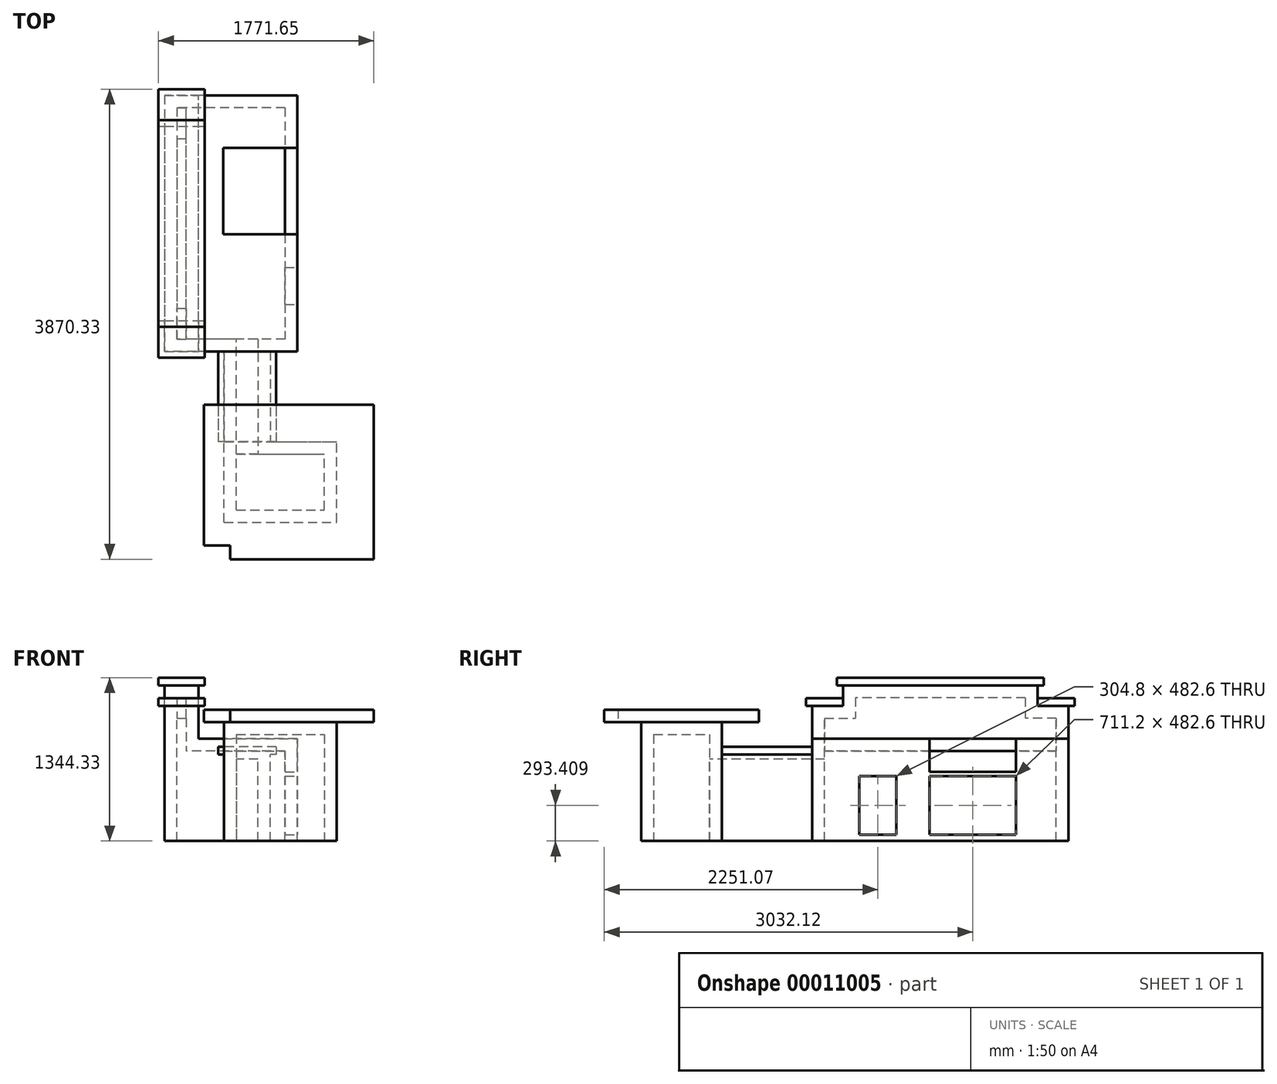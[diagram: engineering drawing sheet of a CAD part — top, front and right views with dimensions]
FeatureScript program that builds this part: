
annotation { "Feature Type Name" : "Feature", "Feature Type Description" : "" }
export const myFeature = defineFeature(function(context is Context, id is Id, definition is map)
    precondition{}
    {
        {
            var Q0;
            Q0=qCreatedBy(makeId("Top.planeOp"),FACE);
            var sketch = newSketch(context, id + "F0", { "sketchPlane" : qUnion([Q0])});
            skLineSegment(sketch, "E0.bottom", {"start": v(0, 0) * mm, "end": v(927.1, 0) * mm});
            skLineSegment(sketch, "E0.top", {"start": v(0, 663.58) * mm, "end": v(927.1, 663.58) * mm});
            skLineSegment(sketch, "E0.left", {"start": v(0, 0) * mm, "end": v(0, 663.57) * mm});
            skLineSegment(sketch, "E0.right", {"start": v(927.1, 0) * mm, "end": v(927.1, 663.57) * mm});
            skLineSegment(sketch, "E1", {"start": v(-165.1, 968.38) * mm, "end": v(1231.9, 968.38) * mm, "construction": true});
            skLineSegment(sketch, "E2", {"start": v(-165.1, 968.38) * mm, "end": v(-165.1, -536.51) * mm, "construction": true});
            skLineSegment(sketch, "E3", {"start": v(1231.9, 968.38) * mm, "end": v(1231.9, -304.8) * mm, "construction": true});
            skLineSegment(sketch, "E4", {"start": v(-360.43, -304.8) * mm, "end": v(1231.9, -304.8) * mm, "construction": true});
            skLineSegment(sketch, "E5", {"start": v(1218.2, -371.79) * mm, "end": v(1218.2, -526.13) * mm, "construction": true});
            skLineSegment(sketch, "E6", {"start": v(-261.75, -190.5) * mm, "end": v(349.74, -190.5) * mm, "construction": true});
            skLineSegment(sketch, "E7", {"start": v(50.8, -83.43) * mm, "end": v(50.8, -408.34) * mm, "construction": true});
            skSolve(sketch);
        }
        {
            var Q0;
            Q0=makeQuery(id+"F0.imprint","IMPRINT",FACE,{"disambiguationData":[TD([[makeQuery(id+"F0.imprint","IMPRINT",EDGE,{"derivedFrom":sQuery(id+"F0.wireOp",EDGE,"E0.bottom")}),1.0]])]});
            extrude(context, id + "F1", {"entities" : qUnion([Q0]), "depth" : 977.9 * mm});
        }
        {
            var Q0;
            Q0=makeQuery(id+"F1.opExtrude","CAP_FACE",FACE,{"disambiguationData":[OSD([sQuery(id+"F0.wireOp",EDGE,"E0.bottom"),sQuery(id+"F0.wireOp",EDGE,"E0.top"),sQuery(id+"F0.wireOp",EDGE,"E0.left"),sQuery(id+"F0.wireOp",EDGE,"E0.right")])],"isStart":false});
            var sketch = newSketch(context, id + "F2", { "sketchPlane" : qUnion([Q0])});
            skLineSegment(sketch, "E8.0", {"start": v(0, 0) * mm, "end": v(927.1, 0) * mm});
            skLineSegment(sketch, "E8.1", {"start": v(0, 663.58) * mm, "end": v(927.1, 663.58) * mm});
            skLineSegment(sketch, "E8.2", {"start": v(0, 0) * mm, "end": v(0, 663.57) * mm});
            skLineSegment(sketch, "E8.3", {"start": v(927.1, 0) * mm, "end": v(927.1, 663.57) * mm});
            skLineSegment(sketch, "E8.4", {"start": v(-165.1, 968.38) * mm, "end": v(1231.9, 968.38) * mm});
            skLineSegment(sketch, "E8.5", {"start": v(-165.1, 968.38) * mm, "end": v(-165.1, -536.51) * mm});
            skLineSegment(sketch, "E8.6", {"start": v(1231.9, 968.38) * mm, "end": v(1231.9, -304.8) * mm});
            skLineSegment(sketch, "E8.7", {"start": v(-360.43, -304.8) * mm, "end": v(1231.9, -304.8) * mm});
            skLineSegment(sketch, "E8.8", {"start": v(1218.2, -371.79) * mm, "end": v(1218.2, -526.13) * mm});
            skLineSegment(sketch, "E8.9", {"start": v(-261.75, -190.5) * mm, "end": v(349.74, -190.5) * mm});
            skLineSegment(sketch, "E8.10", {"start": v(50.8, -83.43) * mm, "end": v(50.8, -408.34) * mm});
            skLineSegment(sketch, "E9", {"start": v(1231.9, 968.38) * mm, "end": v(-165.1, 968.38) * mm});
            skLineSegment(sketch, "E10", {"start": v(-165.1, -190.5) * mm, "end": v(50.8, -190.5) * mm});
            skLineSegment(sketch, "E11", {"start": v(50.8, -190.5) * mm, "end": v(50.8, -304.8) * mm});
            skLineSegment(sketch, "E12", {"start": v(50.8, -304.8) * mm, "end": v(1231.9, -304.8) * mm});
            skPoint(sketch, "E13", {"position": v(927.1, 0) * mm});
            skSolve(sketch);
        }
        {
            var Q0;
            Q0=makeQuery(id+"F2.imprint","IMPRINT",FACE,{"disambiguationData":[TD([[makeQuery(id+"F2.imprint","IMPRINT",EDGE,{"derivedFrom":sQuery(id+"F2.wireOp",EDGE,"E8.0")}),-1.0]])]});
            var Q1;
            Q1=makeQuery(id+"F2.imprint","IMPRINT",FACE,{"disambiguationData":[TD([[makeQuery(id+"F2.imprint","IMPRINT",EDGE,{"derivedFrom":sQuery(id+"F2.wireOp",EDGE,"E8.0")}),1.0]])]});
            extrude(context, id + "F3", {"entities" : qUnion([Q0, Q1]), "depth" : 103.19 * mm});
        }
        {
            var Q0;
            Q0=makeQuery(id+"F1.opExtrude","SWEPT_FACE",FACE,{"disambiguationData":[OSD([sQuery(id+"F0.wireOp",EDGE,"E0.top")])]});
            var sketch = newSketch(context, id + "F4", { "sketchPlane" : qUnion([Q0])});
            skLineSegment(sketch, "E14.bottom", {"start": v(0, 0) * mm, "end": v(-381, 0) * mm});
            skLineSegment(sketch, "E14.top", {"start": v(0, 711.2) * mm, "end": v(-381, 711.2) * mm});
            skLineSegment(sketch, "E14.left", {"start": v(0, 0) * mm, "end": v(0, 711.2) * mm});
            skLineSegment(sketch, "E14.right", {"start": v(-381, 0) * mm, "end": v(-381, 711.2) * mm});
            skLineSegment(sketch, "E15.0", {"start": v(-927.1, 977.9) * mm, "end": v(-927.1, 0) * mm});
            skLineSegment(sketch, "E16.0", {"start": v(0, 977.9) * mm, "end": v(0, 0) * mm});
            skLineSegment(sketch, "E17.0", {"start": v(0, 0) * mm, "end": v(-927.1, 0) * mm});
            skLineSegment(sketch, "E18.0", {"start": v(165.1, 977.9) * mm, "end": v(-1231.9, 977.9) * mm});
            skSolve(sketch);
        }
        {
            var Q0;
            {var subQ4=sQuery(id+"F4.wireOp",EDGE,"E14.top");Q0=makeQuery(id+"F4.imprint","IMPRINT",FACE,{"disambiguationData":[TD([[makeQuery(id+"F4.imprint","IMPRINT",EDGE,{"derivedFrom":subQ4}),1.0]])]});}
            extrude(context, id + "F5", {"entities" : qUnion([Q0]), "operationType" : NewBodyOperationType.ADD, "depth" : 742.95 * mm});
        }
        {
            var Q0;
            Q0=makeQuery(id+"F5.opExtrude","SWEPT_FACE",FACE,{"disambiguationData":[OSD([sQuery(id+"F4.wireOp",EDGE,"E14.top")])]});
            var sketch = newSketch(context, id + "F6", { "sketchPlane" : qUnion([Q0])});
            skLineSegment(sketch, "E19.0", {"start": v(-47.63, 1406.52) * mm, "end": v(-47.63, 663.57) * mm});
            skLineSegment(sketch, "E20.0", {"start": v(428.63, 1406.53) * mm, "end": v(428.63, 663.58) * mm});
            skLineSegment(sketch, "E21.bottom", {"start": v(428.63, 663.58) * mm, "end": v(-47.62, 663.58) * mm});
            skLineSegment(sketch, "E21.top", {"start": v(428.63, 1406.52) * mm, "end": v(-47.62, 1406.52) * mm});
            skLineSegment(sketch, "E21.left", {"start": v(428.63, 663.58) * mm, "end": v(428.63, 1406.52) * mm});
            skLineSegment(sketch, "E21.right", {"start": v(-47.63, 663.58) * mm, "end": v(-47.63, 1406.52) * mm});
            skSolve(sketch);
        }
        {
            var Q0;
            Q0 = qSketchRegion(id + "F6", true);
            extrude(context, id + "F7", {"entities" : qUnion([Q0]), "operationType" : NewBodyOperationType.ADD, "depth" : 63.5 * mm});
        }
        {
            var Q0;
            Q0=makeQuery(id+"F7.boolean.opBoolean","MERGE",FACE,{"derivedFrom":[makeQuery(id+"F5.opExtrude","CAP_FACE",FACE,{"disambiguationData":[OSD([sQuery(id+"F4.wireOp",EDGE,"E14.top"),sQuery(id+"F4.wireOp",EDGE,"E14.right"),sQuery(id+"F4.wireOp",EDGE,"E16.0"),sQuery(id+"F4.wireOp",EDGE,"E17.0")])],"isStart":false}),makeQuery(id+"F7.opExtrude","SWEPT_FACE",FACE,{"disambiguationData":[OSD([sQuery(id+"F6.wireOp",EDGE,"E21.top")])]})]});
            var sketch = newSketch(context, id + "F8", { "sketchPlane" : qUnion([Q0])});
            skLineSegment(sketch, "E22.bottom", {"start": v(-603.25, 0) * mm, "end": v(488.95, 0) * mm});
            skLineSegment(sketch, "E22.top", {"start": v(-603.25, 842.68) * mm, "end": v(488.95, 842.68) * mm});
            skLineSegment(sketch, "E22.left", {"start": v(-603.25, 0) * mm, "end": v(-603.25, 842.68) * mm});
            skLineSegment(sketch, "E22.right", {"start": v(488.95, 0) * mm, "end": v(488.95, 842.68) * mm});
            skLineSegment(sketch, "E23.0", {"start": v(-381, 0) * mm, "end": v(-381, 711.2) * mm});
            skLineSegment(sketch, "E24.0", {"start": v(0, 711.2) * mm, "end": v(0, 0) * mm});
            skSolve(sketch);
        }
        {
            var Q0;
            Q0=makeQuery(id+"F8.imprint","IMPRINT",FACE,{"disambiguationData":[TD([[makeQuery(id+"F8.imprint","IMPRINT",EDGE,{"derivedFrom":sQuery(id+"F8.wireOp",EDGE,"E22.top")}),-1.0]])]});
            var Q1;
            {var subQ10=sQuery(id+"F8.wireOp",EDGE,"E23.0");Q1=makeQuery(id+"F8.imprint","IMPRINT",FACE,{"disambiguationData":[TD([[makeQuery(id+"F8.imprint","IMPRINT",EDGE,{"derivedFrom":subQ10}),-1.0]])]});}
            extrude(context, id + "F9", {"entities" : qUnion([Q0, Q1]), "operationType" : NewBodyOperationType.ADD, "depth" : 2108.2 * mm});
        }
        {
            var Q0;
            Q0=makeQuery(id+"F9.opExtrude","SWEPT_FACE",FACE,{"disambiguationData":[OSD([sQuery(id+"F8.wireOp",EDGE,"E22.top")])]});
            var sketch = newSketch(context, id + "F10", { "sketchPlane" : qUnion([Q0])});
            skLineSegment(sketch, "E25.bottom", {"start": v(-488.95, 1406.53) * mm, "end": v(-209.55, 1406.53) * mm});
            skLineSegment(sketch, "E25.top", {"start": v(-488.95, 3514.73) * mm, "end": v(-209.55, 3514.73) * mm});
            skLineSegment(sketch, "E25.left", {"start": v(-488.95, 1406.53) * mm, "end": v(-488.95, 3514.73) * mm});
            skLineSegment(sketch, "E25.right", {"start": v(-209.55, 1406.53) * mm, "end": v(-209.55, 3514.73) * mm});
            skSolve(sketch);
        }
        {
            var Q0;
            Q0=makeQuery(id+"F10.imprint","IMPRINT",FACE,{"disambiguationData":[TD([[makeQuery(id+"F10.imprint","IMPRINT",EDGE,{"derivedFrom":sQuery(id+"F10.wireOp",EDGE,"E25.bottom")}),-1.0]])]});
            extrude(context, id + "F11", {"entities" : qUnion([Q0]), "operationType" : NewBodyOperationType.ADD, "depth" : 438.15 * mm});
        }
        {
            var Q0;
            Q0=makeQuery(id+"F11.opExtrude","SWEPT_FACE",FACE,{"disambiguationData":[OSD([sQuery(id+"F10.wireOp",EDGE,"E25.right")])]});
            var sketch = newSketch(context, id + "F12", { "sketchPlane" : qUnion([Q0])});
            skLineSegment(sketch, "E26.bottom", {"start": v(3514.73, 1280.83) * mm, "end": v(3260.73, 1280.83) * mm});
            skLineSegment(sketch, "E26.top", {"start": v(3514.73, 1112.56) * mm, "end": v(3260.73, 1112.56) * mm});
            skLineSegment(sketch, "E26.left", {"start": v(3514.73, 1280.83) * mm, "end": v(3514.73, 1112.56) * mm});
            skLineSegment(sketch, "E26.right", {"start": v(3260.73, 1280.83) * mm, "end": v(3260.73, 1112.56) * mm});
            skLineSegment(sketch, "E27.bottom", {"start": v(1406.53, 1280.83) * mm, "end": v(1660.53, 1280.83) * mm});
            skLineSegment(sketch, "E27.top", {"start": v(1406.53, 1112.56) * mm, "end": v(1660.53, 1112.56) * mm});
            skLineSegment(sketch, "E27.left", {"start": v(1406.53, 1280.83) * mm, "end": v(1406.53, 1112.56) * mm});
            skLineSegment(sketch, "E27.right", {"start": v(1660.53, 1280.83) * mm, "end": v(1660.53, 1112.56) * mm});
            skSolve(sketch);
        }
        {
            var Q0;
            Q0=makeQuery(id+"F12.imprint","IMPRINT",FACE,{"disambiguationData":[TD([[makeQuery(id+"F12.imprint","IMPRINT",EDGE,{"derivedFrom":sQuery(id+"F12.wireOp",EDGE,"E27.bottom")}),-1.0]])]});
            var Q1;
            Q1=makeQuery(id+"F12.imprint","IMPRINT",FACE,{"disambiguationData":[TD([[makeQuery(id+"F12.imprint","IMPRINT",EDGE,{"derivedFrom":sQuery(id+"F12.wireOp",EDGE,"E26.bottom")}),-1.0]])]});
            extrude(context, id + "F13", {"entities" : qUnion([Q0, Q1]), "operationType" : NewBodyOperationType.REMOVE, "oppositeDirection" : true, "depth" : 279.4 * mm, "hasSecondDirection" : true, "secondDirectionOppositeDirection" : false, "secondDirectionDepth" : 25.4 * mm});
        }
        {
            var Q0;
            Q0=makeQuery(id+"F9.opExtrude","SWEPT_FACE",FACE,{"disambiguationData":[OSD([sQuery(id+"F8.wireOp",EDGE,"E22.left")])]});
            var sketch = newSketch(context, id + "F14", { "sketchPlane" : qUnion([Q0])});
            skLineSegment(sketch, "E28.bottom", {"start": v(1793.88, 534.7) * mm, "end": v(2098.68, 534.7) * mm});
            skLineSegment(sketch, "E28.top", {"start": v(1793.88, 52.1) * mm, "end": v(2098.68, 52.1) * mm});
            skLineSegment(sketch, "E28.left", {"start": v(1793.88, 534.7) * mm, "end": v(1793.88, 52.1) * mm});
            skLineSegment(sketch, "E28.right", {"start": v(2098.68, 534.7) * mm, "end": v(2098.68, 52.1) * mm});
            skLineSegment(sketch, "E29.bottom", {"start": v(2371.73, 534.7) * mm, "end": v(3082.93, 534.7) * mm});
            skLineSegment(sketch, "E29.top", {"start": v(2371.73, 52.1) * mm, "end": v(3082.93, 52.1) * mm});
            skLineSegment(sketch, "E29.left", {"start": v(2371.73, 534.7) * mm, "end": v(2371.73, 52.1) * mm});
            skLineSegment(sketch, "E29.right", {"start": v(3082.93, 534.7) * mm, "end": v(3082.93, 52.1) * mm});
            skLineSegment(sketch, "E30", {"start": v(1812.94, 52.1) * mm, "end": v(3421.73, 52.1) * mm, "construction": true});
            skLineSegment(sketch, "E31.bottom", {"start": v(2371.73, 842.68) * mm, "end": v(3082.93, 842.68) * mm});
            skLineSegment(sketch, "E31.top", {"start": v(2371.73, 569.63) * mm, "end": v(3082.93, 569.63) * mm});
            skLineSegment(sketch, "E31.left", {"start": v(2371.73, 842.68) * mm, "end": v(2371.73, 569.63) * mm});
            skLineSegment(sketch, "E31.right", {"start": v(3082.93, 842.68) * mm, "end": v(3082.93, 569.63) * mm});
            skSolve(sketch);
        }
        {
            var Q0;
            Q0=makeQuery(id+"F9.boolean.opBoolean","MERGE",FACE,{"derivedFrom":[makeQuery(id+"F5.boolean.opBoolean","MERGE",FACE,{"derivedFrom":[makeQuery(id+"F1.opExtrude","CAP_FACE",FACE,{"disambiguationData":[OSD([sQuery(id+"F0.wireOp",EDGE,"E0.bottom"),sQuery(id+"F0.wireOp",EDGE,"E0.top"),sQuery(id+"F0.wireOp",EDGE,"E0.left"),sQuery(id+"F0.wireOp",EDGE,"E0.right")])],"isStart":true}),makeQuery(id+"F5.opExtrude","SWEPT_FACE",FACE,{"disambiguationData":[OSD([sQuery(id+"F4.wireOp",EDGE,"E17.0")])]})]}),makeQuery(id+"F9.opExtrude","SWEPT_FACE",FACE,{"disambiguationData":[OSD([sQuery(id+"F8.wireOp",EDGE,"E22.bottom")])]})]});
            shell(context, id + "F15", {"entities" : qUnion([Q0]), "thickness" : 101.6 * mm});
        }
        {
            var Q0;
            Q0=makeQuery(id+"F14.imprint","IMPRINT",FACE,{"disambiguationData":[TD([[makeQuery(id+"F14.imprint","IMPRINT",EDGE,{"derivedFrom":sQuery(id+"F14.wireOp",EDGE,"E28.bottom")}),-1.0]])]});
            extrude(context, id + "F16", {"entities" : qUnion([Q0]), "operationType" : NewBodyOperationType.REMOVE, "oppositeDirection" : true, "depth" : 101.6 * mm});
        }
        {
            var Q0;
            Q0=makeQuery(id+"F14.imprint","IMPRINT",FACE,{"disambiguationData":[TD([[makeQuery(id+"F14.imprint","IMPRINT",EDGE,{"derivedFrom":sQuery(id+"F14.wireOp",EDGE,"E29.bottom")}),-1.0]])]});
            extrude(context, id + "F17", {"entities" : qUnion([Q0]), "operationType" : NewBodyOperationType.REMOVE, "oppositeDirection" : true, "depth" : 101.6 * mm});
        }
        {
            var Q0;
            Q0=makeQuery(id+"F14.imprint","IMPRINT",FACE,{"disambiguationData":[TD([[makeQuery(id+"F14.imprint","IMPRINT",EDGE,{"derivedFrom":sQuery(id+"F14.wireOp",EDGE,"E31.bottom")}),1.0]])]});
            extrude(context, id + "F18", {"entities" : qUnion([Q0]), "operationType" : NewBodyOperationType.REMOVE, "oppositeDirection" : true, "depth" : 609.6 * mm});
        }
        {
            var Q0;
            Q0=makeQuery(id+"F13.boolean.opBoolean","COPY",FACE,{"derivedFrom":makeQuery(id+"F13.opExtrude","SWEPT_FACE",FACE,{"disambiguationData":[OSD([sQuery(id+"F12.wireOp",EDGE,"E26.top")])]})});
            var sketch = newSketch(context, id + "F19", { "sketchPlane" : qUnion([Q0])});
            skLineSegment(sketch, "E32", {"start": v(-349.25, 3514.73) * mm, "end": v(-349.25, 3260.73) * mm, "construction": true});
            skLineSegment(sketch, "E33.bottom", {"start": v(-349.25, 3260.73) * mm, "end": v(-539.75, 3260.73) * mm});
            skLineSegment(sketch, "E33.top", {"start": v(-349.25, 3565.53) * mm, "end": v(-539.75, 3565.53) * mm});
            skLineSegment(sketch, "E33.left", {"start": v(-349.25, 3260.73) * mm, "end": v(-349.25, 3565.53) * mm});
            skLineSegment(sketch, "E33.right", {"start": v(-539.75, 3260.73) * mm, "end": v(-539.75, 3565.53) * mm});
            skLineSegment(sketch, "E34.0.MirrorCS", {"start": v(-349.25, 3260.73) * mm, "end": v(-158.75, 3260.73) * mm});
            skLineSegment(sketch, "E35.0.MirrorCS", {"start": v(-158.75, 3260.73) * mm, "end": v(-158.75, 3565.53) * mm});
            skLineSegment(sketch, "E36.0.MirrorCS", {"start": v(-349.25, 3565.53) * mm, "end": v(-158.75, 3565.53) * mm});
            skSolve(sketch);
        }
        {
            var Q0;
            Q0 = qSketchRegion(id + "F19", true);
            extrude(context, id + "F20", {"entities" : qUnion([Q0]), "operationType" : NewBodyOperationType.ADD, "depth" : 63.5 * mm});
        }
        {
            var Q0;
            Q0=makeQuery(id+"F13.boolean.opBoolean","COPY",FACE,{"derivedFrom":makeQuery(id+"F13.opExtrude","SWEPT_FACE",FACE,{"disambiguationData":[OSD([sQuery(id+"F12.wireOp",EDGE,"E27.top")])]})});
            var sketch = newSketch(context, id + "F21", { "sketchPlane" : qUnion([Q0])});
            skLineSegment(sketch, "E37", {"start": v(-349.25, 1406.53) * mm, "end": v(-349.25, 1660.53) * mm});
            skLineSegment(sketch, "E38.bottom", {"start": v(-349.25, 1660.53) * mm, "end": v(-539.75, 1660.53) * mm});
            skLineSegment(sketch, "E38.top", {"start": v(-349.25, 1355.73) * mm, "end": v(-539.75, 1355.73) * mm});
            skLineSegment(sketch, "E38.left", {"start": v(-349.25, 1660.53) * mm, "end": v(-349.25, 1355.73) * mm});
            skLineSegment(sketch, "E38.right", {"start": v(-539.75, 1660.53) * mm, "end": v(-539.75, 1355.73) * mm});
            skLineSegment(sketch, "E39.0.MirrorCS", {"start": v(-349.25, 1355.73) * mm, "end": v(-158.75, 1355.73) * mm});
            skLineSegment(sketch, "E40.0.MirrorCS", {"start": v(-158.75, 1660.53) * mm, "end": v(-158.75, 1355.73) * mm});
            skLineSegment(sketch, "E41.0.MirrorCS", {"start": v(-349.25, 1660.53) * mm, "end": v(-158.75, 1660.53) * mm});
            skSolve(sketch);
        }
        {
            var Q0;
            Q0 = qSketchRegion(id + "F21", true);
            extrude(context, id + "F22", {"entities" : qUnion([Q0]), "operationType" : NewBodyOperationType.ADD, "depth" : 63.5 * mm});
        }
        {
            var Q0;
            Q0=makeQuery(id+"F11.opExtrude","CAP_FACE",FACE,{"disambiguationData":[OSD([sQuery(id+"F10.wireOp",EDGE,"E25.bottom"),sQuery(id+"F10.wireOp",EDGE,"E25.top"),sQuery(id+"F10.wireOp",EDGE,"E25.left"),sQuery(id+"F10.wireOp",EDGE,"E25.right")])],"isStart":false});
            var sketch = newSketch(context, id + "F23", { "sketchPlane" : qUnion([Q0])});
            skLineSegment(sketch, "E42.bottom", {"start": v(-158.75, 3311.53) * mm, "end": v(-539.75, 3311.53) * mm});
            skLineSegment(sketch, "E42.top", {"start": v(-158.75, 1609.73) * mm, "end": v(-539.75, 1609.73) * mm});
            skLineSegment(sketch, "E42.left", {"start": v(-158.75, 3311.53) * mm, "end": v(-158.75, 1609.73) * mm});
            skLineSegment(sketch, "E42.right", {"start": v(-539.75, 3311.53) * mm, "end": v(-539.75, 1609.73) * mm});
            skSolve(sketch);
        }
        {
            var Q0;
            Q0=makeQuery(id+"F23.imprint","IMPRINT",FACE,{"disambiguationData":[TD([[makeQuery(id+"F23.imprint","IMPRINT",EDGE,{"derivedFrom":makeQuery(id+"F11.opExtrude","CAP_EDGE",EDGE,{"disambiguationData":[OSD([sQuery(id+"F10.wireOp",EDGE,"E25.left")])],"isStart":false})}),1.0]])]});
            var Q1;
            Q1=makeQuery(id+"F23.imprint","IMPRINT",FACE,{"disambiguationData":[TD([[makeQuery(id+"F23.imprint","IMPRINT",EDGE,{"derivedFrom":sQuery(id+"F23.wireOp",EDGE,"E42.bottom")}),1.0]])]});
            extrude(context, id + "F24", {"entities" : qUnion([Q0, Q1]), "operationType" : NewBodyOperationType.ADD, "depth" : 63.5 * mm});
        }
    });
